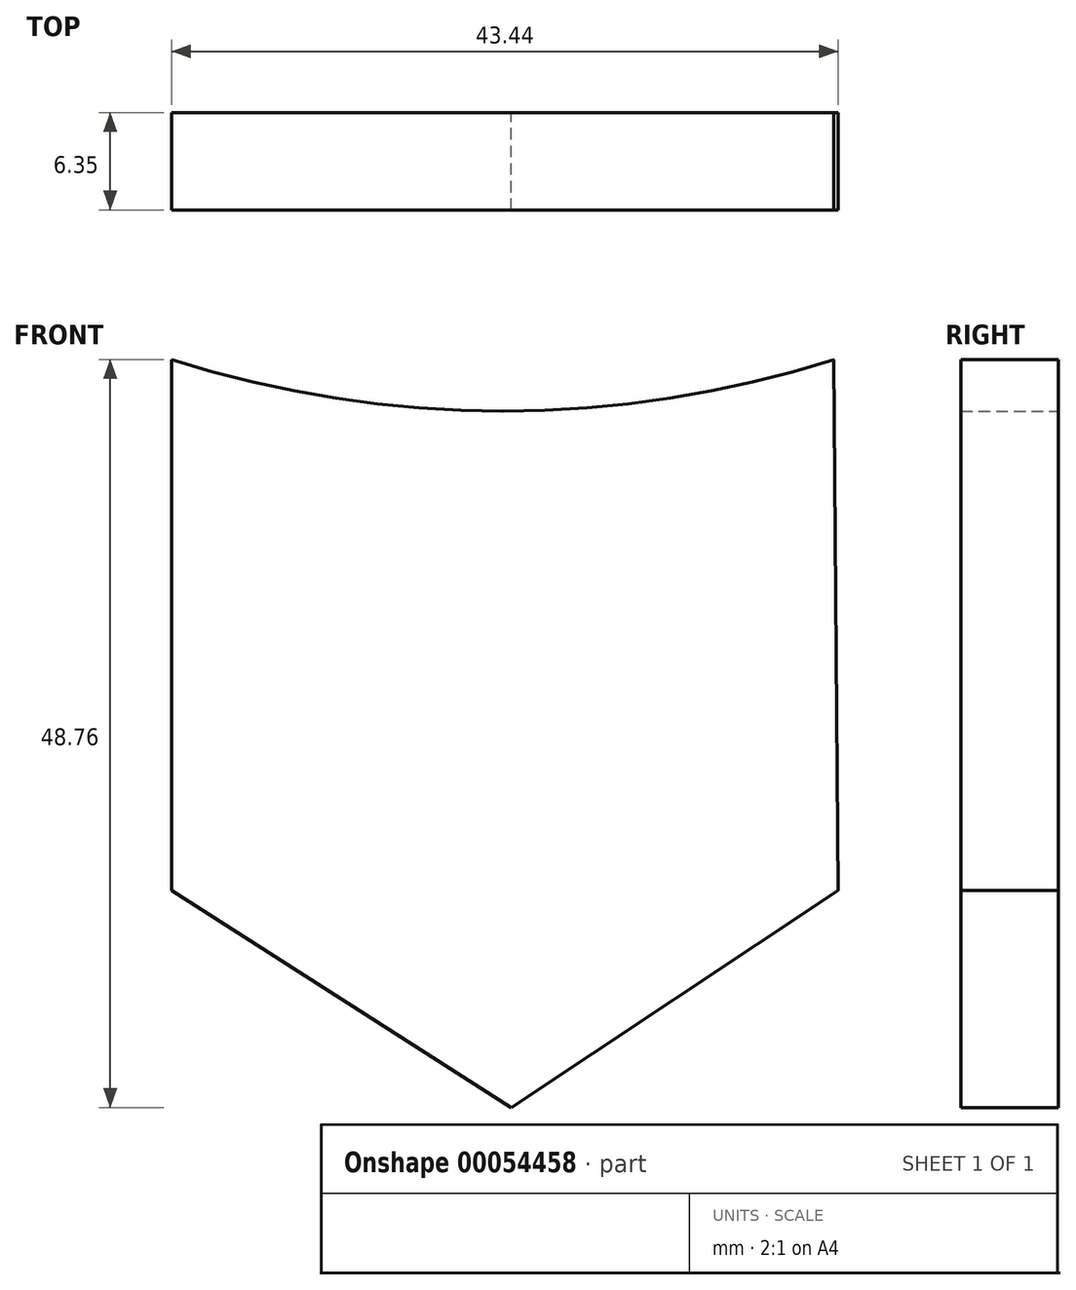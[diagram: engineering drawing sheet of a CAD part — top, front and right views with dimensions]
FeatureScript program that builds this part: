
annotation { "Feature Type Name" : "Feature", "Feature Type Description" : "" }
export const myFeature = defineFeature(function(context is Context, id is Id, definition is map)
    precondition{}
    {
        {
            var Q0;
            Q0=qCreatedBy(makeId("Front.planeOp"),FACE);
            var sketch = newSketch(context, id + "F0", { "sketchPlane" : qUnion([Q0])});
            skArc(sketch, "E0", {"start": v(-22.14, 34.61) * mm, "mid": v(-0.56, 31.25) * mm, "end": v(21.02, 34.61) * mm});
            skLineSegment(sketch, "E1", {"start": v(-22.14, 34.61) * mm, "end": v(-22.14, 0) * mm});
            skLineSegment(sketch, "E2", {"start": v(-22.14, 0) * mm, "end": v(0, -14.15) * mm});
            skLineSegment(sketch, "E3", {"start": v(0, -14.15) * mm, "end": v(21.3, 0) * mm});
            skLineSegment(sketch, "E4", {"start": v(21.3, 0) * mm, "end": v(21.02, 34.61) * mm});
            skSolve(sketch);
        }
        {
            var Q0;
            Q0=makeQuery(id+"F0.imprint","IMPRINT",FACE,{"disambiguationData":[TD([[makeQuery(id+"F0.imprint","IMPRINT",EDGE,{"derivedFrom":sQuery(id+"F0.wireOp",EDGE,"E0")}),-1.0]])]});
            extrude(context, id + "F1", {"entities" : qUnion([Q0]), "depth" : 6.35 * mm});
        }
    });
